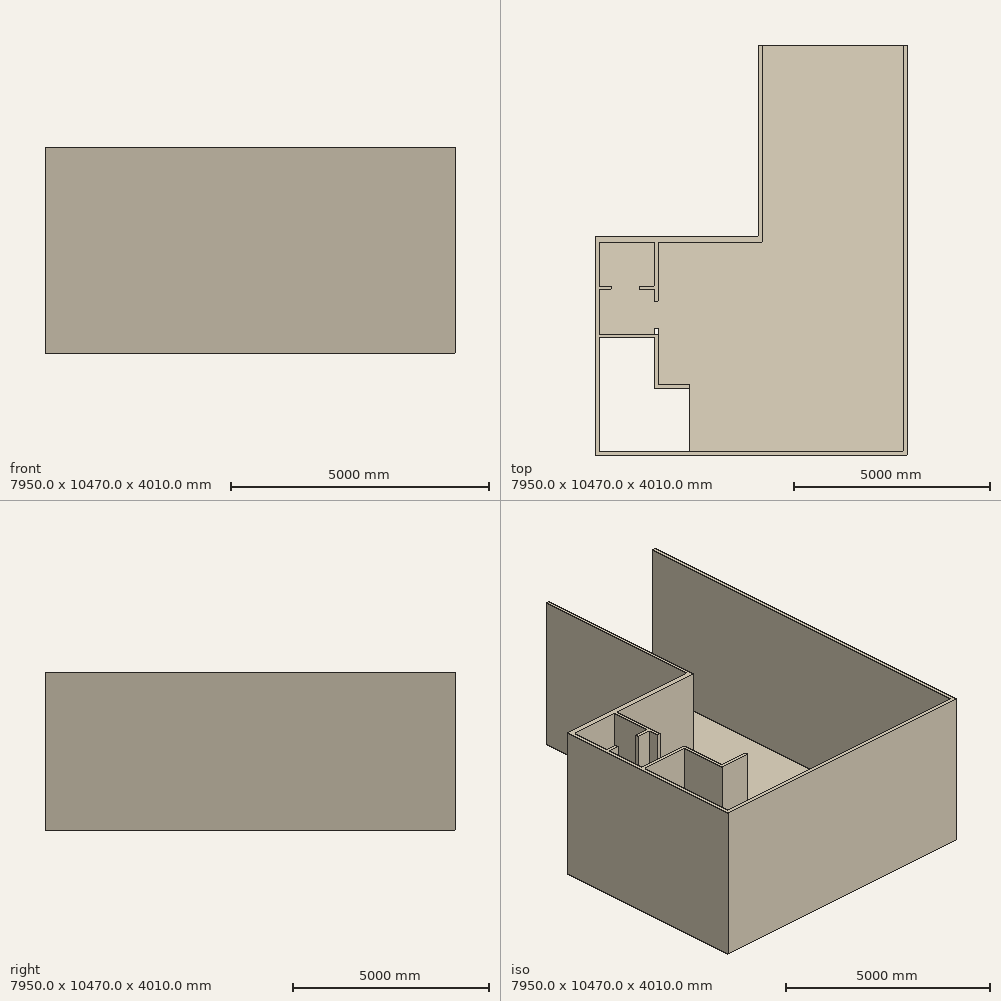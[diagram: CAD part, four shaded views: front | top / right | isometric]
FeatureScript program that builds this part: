
annotation { "Feature Type Name" : "Feature", "Feature Type Description" : "" }
export const myFeature = defineFeature(function(context is Context, id is Id, definition is map)
    precondition{}
    {
        {
            var Q0;
            Q0=qCreatedBy(makeId("Top.planeOp"),FACE);
            var sketch = newSketch(context, id + "F0", { "sketchPlane" : qUnion([Q0])});
            skLineSegment(sketch, "E0.bottom", {"start": v(0, 0) * mm, "end": v(20000, 0) * mm, "construction": true});
            skLineSegment(sketch, "E0.top", {"start": v(0, 30000) * mm, "end": v(20000, 30000) * mm, "construction": true});
            skLineSegment(sketch, "E0.left", {"start": v(0, 0) * mm, "end": v(0, 30000) * mm, "construction": true});
            skLineSegment(sketch, "E0.right", {"start": v(20000, 0) * mm, "end": v(20000, 30000) * mm, "construction": true});
            skLineSegment(sketch, "E1.bottom", {"start": v(0, 0) * mm, "end": v(200, 0) * mm, "construction": true});
            skLineSegment(sketch, "E1.top", {"start": v(0, 200) * mm, "end": v(200, 200) * mm, "construction": true});
            skLineSegment(sketch, "E1.left", {"start": v(0, 0) * mm, "end": v(0, 200) * mm, "construction": true});
            skLineSegment(sketch, "E1.right", {"start": v(200, 0) * mm, "end": v(200, 200) * mm, "construction": true});
            skSolve(sketch);
        }
        {
            var Q0;
            Q0=qCreatedBy(makeId("Top.planeOp"),FACE);
            var sketch = newSketch(context, id + "F1", { "sketchPlane" : qUnion([Q0])});
            skLineSegment(sketch, "E2.bottom", {"start": v(200, 200) * mm, "end": v(7950, 200) * mm});
            skLineSegment(sketch, "E2.top", {"start": v(4250, 10570) * mm, "end": v(7950, 10570) * mm});
            skLineSegment(sketch, "E2.left", {"start": v(200, 200) * mm, "end": v(200, 5693.81) * mm});
            skLineSegment(sketch, "E2.right", {"start": v(7950, 200) * mm, "end": v(7950, 10570) * mm});
            skLineSegment(sketch, "E3.bottom", {"start": v(4250, 10570) * mm, "end": v(4350, 10570) * mm, "construction": true});
            skLineSegment(sketch, "E3.top", {"start": v(200, 5540) * mm, "end": v(4350, 5540) * mm});
            skLineSegment(sketch, "E3.left", {"start": v(200, 5693.81) * mm, "end": v(200, 5540) * mm});
            skLineSegment(sketch, "E3.right", {"start": v(4350, 10570) * mm, "end": v(4350, 5540) * mm});
            skLineSegment(sketch, "E4.bottom", {"start": v(1600, 1810.5) * mm, "end": v(1690, 1810.5) * mm});
            skLineSegment(sketch, "E4.top", {"start": v(1600, 3110) * mm, "end": v(1690, 3110) * mm});
            skLineSegment(sketch, "E4.left", {"start": v(1600, 1810.5) * mm, "end": v(1600, 3110) * mm});
            skLineSegment(sketch, "E4.right", {"start": v(1690, 1810.5) * mm, "end": v(1690, 3110) * mm});
            skLineSegment(sketch, "E5.bottom", {"start": v(1690, 1810.5) * mm, "end": v(2500, 1810.5) * mm});
            skLineSegment(sketch, "E5.top", {"start": v(1690, 1900.5) * mm, "end": v(2500, 1900.5) * mm});
            skLineSegment(sketch, "E5.left", {"start": v(1690, 1810.5) * mm, "end": v(1690, 1900.5) * mm});
            skLineSegment(sketch, "E5.right", {"start": v(2500, 1810.5) * mm, "end": v(2500, 1900.5) * mm});
            skLineSegment(sketch, "E6", {"start": v(300, 3110) * mm, "end": v(300, 300) * mm});
            skLineSegment(sketch, "E7", {"start": v(300, 300) * mm, "end": v(2500, 300) * mm});
            skLineSegment(sketch, "E8", {"start": v(2500, 300) * mm, "end": v(2500, 200) * mm});
            skLineSegment(sketch, "E9.bottom", {"start": v(1690, 3110) * mm, "end": v(200, 3110) * mm});
            skLineSegment(sketch, "E9.top", {"start": v(1690, 3200) * mm, "end": v(200, 3200) * mm});
            skLineSegment(sketch, "E9.left", {"start": v(1690, 3110) * mm, "end": v(1690, 3200) * mm});
            skLineSegment(sketch, "E9.right", {"start": v(200, 3110) * mm, "end": v(200, 3200) * mm});
            skLineSegment(sketch, "E10.bottom", {"start": v(1690, 3200) * mm, "end": v(1600, 3200) * mm});
            skLineSegment(sketch, "E10.top", {"start": v(1690, 3344.77) * mm, "end": v(1600, 3344.77) * mm});
            skLineSegment(sketch, "E10.left", {"start": v(1690, 3200) * mm, "end": v(1690, 3344.77) * mm});
            skLineSegment(sketch, "E10.right", {"start": v(1600, 3200) * mm, "end": v(1600, 3344.77) * mm});
            skLineSegment(sketch, "E11.bottom", {"start": v(1600, 4044.77) * mm, "end": v(1690, 4044.77) * mm});
            skLineSegment(sketch, "E11.top", {"start": v(1600, 5540) * mm, "end": v(1690, 5540) * mm});
            skLineSegment(sketch, "E11.left", {"start": v(1600, 4044.77) * mm, "end": v(1600, 5540) * mm});
            skLineSegment(sketch, "E11.right", {"start": v(1690, 4044.77) * mm, "end": v(1690, 5540) * mm});
            skLineSegment(sketch, "E12.bottom", {"start": v(1600, 4330) * mm, "end": v(1204.23, 4330) * mm});
            skLineSegment(sketch, "E12.top", {"start": v(1600, 4420) * mm, "end": v(1204.23, 4420) * mm});
            skLineSegment(sketch, "E12.left", {"start": v(1600, 4330) * mm, "end": v(1600, 4420) * mm});
            skLineSegment(sketch, "E12.right", {"start": v(1204.23, 4330) * mm, "end": v(1204.23, 4420) * mm});
            skLineSegment(sketch, "E13.bottom", {"start": v(504.23, 4420) * mm, "end": v(200, 4420) * mm});
            skLineSegment(sketch, "E13.top", {"start": v(504.23, 4330) * mm, "end": v(200, 4330) * mm});
            skLineSegment(sketch, "E13.left", {"start": v(504.23, 4420) * mm, "end": v(504.23, 4330) * mm});
            skLineSegment(sketch, "E13.right", {"start": v(200, 4420) * mm, "end": v(200, 4330) * mm});
            skLineSegment(sketch, "E14.0", {"start": v(4250, 10570) * mm, "end": v(4250, 5693.81) * mm});
            skLineSegment(sketch, "E14.3", {"start": v(200, 5693.81) * mm, "end": v(4250, 5693.81) * mm});
            skLineSegment(sketch, "E15.0", {"start": v(8050, 100) * mm, "end": v(8050, 10570) * mm});
            skLineSegment(sketch, "E15.1", {"start": v(100, 100) * mm, "end": v(8050, 100) * mm});
            skLineSegment(sketch, "E15.2", {"start": v(100, 100) * mm, "end": v(100, 5693.81) * mm});
            skLineSegment(sketch, "E16", {"start": v(7950, 10570) * mm, "end": v(8050, 10570) * mm});
            skLineSegment(sketch, "E17.bottom", {"start": v(7950, 10570) * mm, "end": v(4350, 10570) * mm});
            skLineSegment(sketch, "E17.top", {"start": v(7950, 12500.48) * mm, "end": v(4350, 12500.48) * mm});
            skLineSegment(sketch, "E17.left", {"start": v(7950, 10570) * mm, "end": v(7950, 12500.48) * mm});
            skLineSegment(sketch, "E17.right", {"start": v(4350, 10570) * mm, "end": v(4350, 12500.48) * mm});
            skLineSegment(sketch, "E18.bottom", {"start": v(8050, 10570) * mm, "end": v(7950, 10570) * mm, "construction": true});
            skLineSegment(sketch, "E18.top", {"start": v(8050, 12500.48) * mm, "end": v(7950, 12500.48) * mm});
            skLineSegment(sketch, "E18.left", {"start": v(8050, 10570) * mm, "end": v(8050, 12500.48) * mm});
            skLineSegment(sketch, "E19", {"start": v(200, 5693.81) * mm, "end": v(100, 5693.81) * mm});
            skLineSegment(sketch, "E20", {"start": v(2500, 1810.5) * mm, "end": v(2500, 200) * mm});
            skPoint(sketch, "E21.start.orphan", {"position": v(100, 10570) * mm});
            skPoint(sketch, "E22.orphan", {"position": v(200, 10570) * mm});
            skSolve(sketch);
        }
        {
            var Q0;
            {var subQ16=sQuery(id+"F1.wireOp",EDGE,"E2.right");Q0=makeQuery(id+"F1.imprint","IMPRINT",FACE,{"disambiguationData":[TD([[makeQuery(id+"F1.imprint","IMPRINT",EDGE,{"derivedFrom":subQ16}),1.0]])]});}
            extrude(context, id + "F2", {"entities" : qUnion([Q0]), "oppositeDirection" : true, "depth" : 10 * mm});
        }
        {
            var Q0;
            {var subQ4=sQuery(id+"F1.wireOp",EDGE,"E3.right");Q0=makeQuery(id+"F1.imprint","IMPRINT",FACE,{"disambiguationData":[TD([[makeQuery(id+"F1.imprint","IMPRINT",EDGE,{"derivedFrom":subQ4}),-1.0]])]});}
            var Q1;
            {var subQ1=sQuery(id+"F1.wireOp",EDGE,"E11.bottom");Q1=makeQuery(id+"F1.imprint","IMPRINT",FACE,{"disambiguationData":[TD([[makeQuery(id+"F1.imprint","IMPRINT",EDGE,{"derivedFrom":subQ1}),1.0]])]});}
            var Q2;
            Q2=makeQuery(id+"F1.imprint","IMPRINT",FACE,{"disambiguationData":[TD([[makeQuery(id+"F1.imprint","IMPRINT",EDGE,{"derivedFrom":sQuery(id+"F1.wireOp",EDGE,"E12.bottom")}),-1.0]])]});
            var Q3;
            Q3=makeQuery(id+"F1.imprint","IMPRINT",FACE,{"disambiguationData":[TD([[makeQuery(id+"F1.imprint","IMPRINT",EDGE,{"derivedFrom":sQuery(id+"F1.wireOp",EDGE,"E13.bottom")}),1.0]])]});
            var Q4;
            {var subQ6=sQuery(id+"F1.wireOp",EDGE,"E2.right");Q4=makeQuery(id+"F1.imprint","IMPRINT",FACE,{"disambiguationData":[TD([[makeQuery(id+"F1.imprint","IMPRINT",EDGE,{"derivedFrom":subQ6}),-1.0]])]});}
            var Q5;
            Q5=makeQuery(id+"F1.imprint","IMPRINT",FACE,{"disambiguationData":[TD([[makeQuery(id+"F1.imprint","IMPRINT",EDGE,{"derivedFrom":sQuery(id+"F1.wireOp",EDGE,"E5.bottom")}),1.0]])]});
            var Q6;
            Q6=makeQuery(id+"F1.imprint","IMPRINT",FACE,{"disambiguationData":[TD([[makeQuery(id+"F1.imprint","IMPRINT",EDGE,{"derivedFrom":sQuery(id+"F1.wireOp",EDGE,"E4.bottom")}),1.0]])]});
            var Q7;
            Q7=makeQuery(id+"F1.imprint","IMPRINT",FACE,{"disambiguationData":[TD([[makeQuery(id+"F1.imprint","IMPRINT",EDGE,{"derivedFrom":sQuery(id+"F1.wireOp",EDGE,"E9.top")}),1.0]])]});
            var Q8;
            Q8=makeQuery(id+"F1.imprint","IMPRINT",FACE,{"disambiguationData":[TD([[makeQuery(id+"F1.imprint","IMPRINT",EDGE,{"derivedFrom":sQuery(id+"F1.wireOp",EDGE,"E10.bottom")}),-1.0]])]});
            extrude(context, id + "F3", {"entities" : qUnion([Q0, Q1, Q2, Q3, Q4, Q5, Q6, Q7, Q8]), "operationType" : NewBodyOperationType.ADD, "depth" : 4000 * mm, "hasSecondDirection" : true, "secondDirectionOppositeDirection" : true, "secondDirectionDepth" : 10 * mm});
        }
    });
